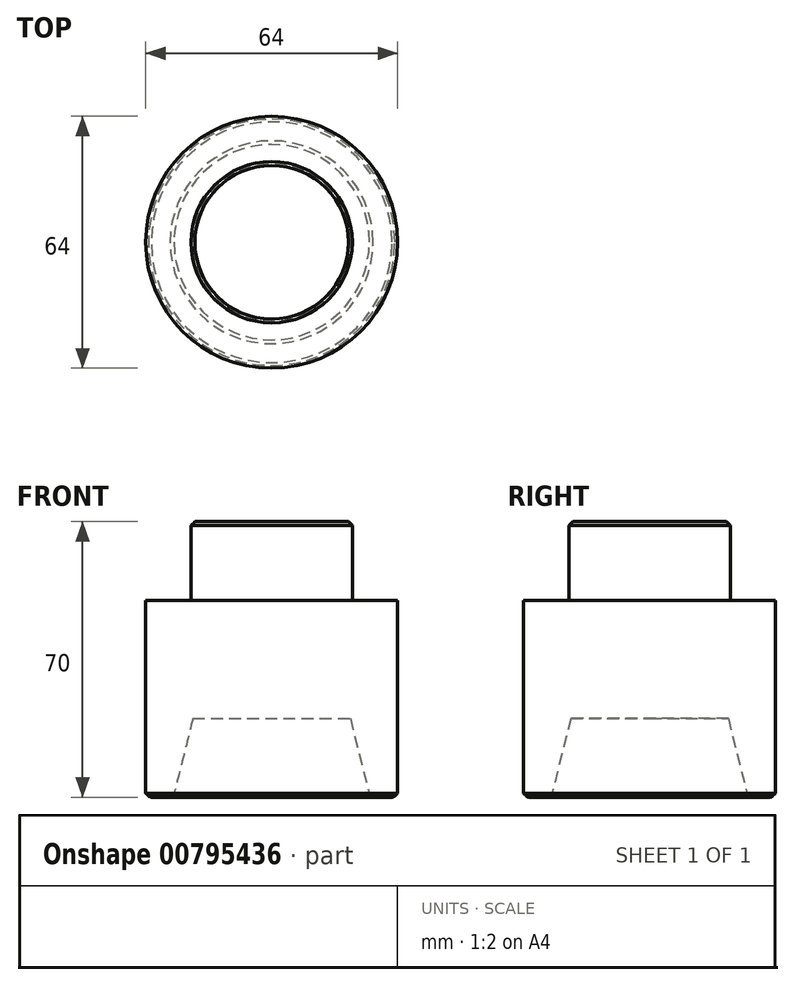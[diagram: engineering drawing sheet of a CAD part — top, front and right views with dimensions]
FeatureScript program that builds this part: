
annotation { "Feature Type Name" : "Feature", "Feature Type Description" : "" }
export const myFeature = defineFeature(function(context is Context, id is Id, definition is map)
    precondition{}
    {
        {
            var Q0;
            Q0=qCreatedBy(makeId("Front.planeOp"),FACE);
            var sketch = newSketch(context, id + "F0", { "sketchPlane" : qUnion([Q0])});
            skLineSegment(sketch, "E0.bottom", {"start": v(25, 0) * mm, "end": v(32, 0) * mm});
            skLineSegment(sketch, "E0.top", {"start": v(20.5, 50) * mm, "end": v(32, 50) * mm});
            skLineSegment(sketch, "E0.left", {"start": v(0, 20) * mm, "end": v(0, 50) * mm});
            skLineSegment(sketch, "E0.right", {"start": v(32, 0) * mm, "end": v(32, 50) * mm});
            skLineSegment(sketch, "E1.top", {"start": v(0, 70) * mm, "end": v(20.5, 70) * mm});
            skLineSegment(sketch, "E1.left", {"start": v(0, 50) * mm, "end": v(0, 70) * mm});
            skLineSegment(sketch, "E1.right", {"start": v(20.5, 50) * mm, "end": v(20.5, 70) * mm});
            skLineSegment(sketch, "E2", {"start": v(0, 20) * mm, "end": v(20, 20) * mm});
            skLineSegment(sketch, "E3", {"start": v(20, 20) * mm, "end": v(25, 0) * mm});
            skSolve(sketch);
        }
        {
            var Q0;
            Q0=makeQuery(id+"F0.imprint","IMPRINT",FACE,{"disambiguationData":[TD([[makeQuery(id+"F0.imprint","IMPRINT",EDGE,{"derivedFrom":sQuery(id+"F0.wireOp",EDGE,"E0.bottom")}),1.0]])]});
            var Q1;
            Q1=sQuery(id+"F0.wireOp",EDGE,"E0.left");
            revolve(context, id + "F1", {"surfaceOperationType" : NewSurfaceOperationType.NEW, "entities" : qUnion([Q0]), "axis" : qUnion([Q1]), "revolveType" : RevolveType.FULL});
        }
        {
            var Q0;
            Q0=makeQuery(id+"F1.opRevolve","SWEPT_EDGE",EDGE,{"disambiguationData":[OSD([sQuery(id+"F0.wireOp",EDGE,"E0.bottom"),sQuery(id+"F0.wireOp",EDGE,"E0.right")])]});
            var Q1;
            Q1=makeQuery(id+"F1.opRevolve","SWEPT_EDGE",EDGE,{"disambiguationData":[OSD([sQuery(id+"F0.wireOp",EDGE,"E1.top"),sQuery(id+"F0.wireOp",EDGE,"E1.right")])]});
            chamfer(context, id + "F2", {"entities" : qUnion([Q0, Q1]), "width" : 1 * mm, "tangentPropagation" : true});
        }
        {
            var Q0;
            Q0=makeQuery(id+"F1.opRevolve","SWEPT_FACE",FACE,{"disambiguationData":[OSD([sQuery(id+"F0.wireOp",EDGE,"E0.bottom")])]});
            chamfer(context, id + "F3", {"entities" : qUnion([Q0]), "width" : 1 * mm, "tangentPropagation" : true});
        }
    });
